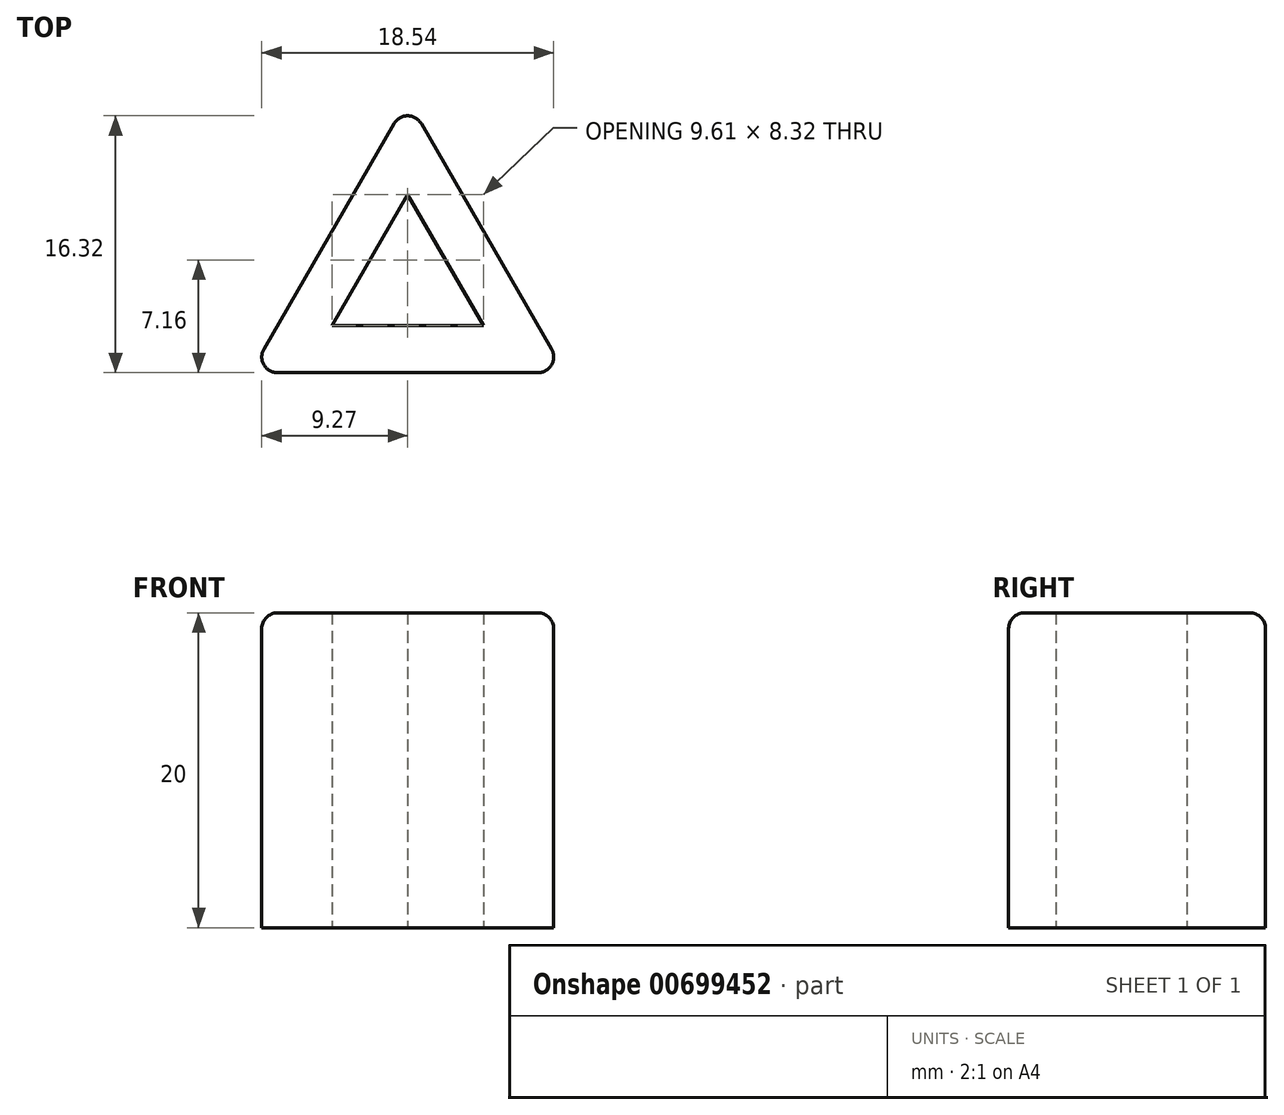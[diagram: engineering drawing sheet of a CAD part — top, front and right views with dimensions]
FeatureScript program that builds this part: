
annotation { "Feature Type Name" : "Feature", "Feature Type Description" : "" }
export const myFeature = defineFeature(function(context is Context, id is Id, definition is map)
    precondition{}
    {
        {
            var Q0;
            Q0=qCreatedBy(makeId("Top.planeOp"),FACE);
            var sketch = newSketch(context, id + "F0", { "sketchPlane" : qUnion([Q0])});
            skLineSegment(sketch, "E0.bottom", {"start": v(10, 10) * mm, "end": v(-10, 10) * mm, "construction": true});
            skLineSegment(sketch, "E0.top", {"start": v(10, -10) * mm, "end": v(-10, -10) * mm, "construction": true});
            skLineSegment(sketch, "E0.left", {"start": v(10, 10) * mm, "end": v(10, -10) * mm, "construction": true});
            skLineSegment(sketch, "E0.right", {"start": v(-10, 10) * mm, "end": v(-10, -10) * mm, "construction": true});
            skPoint(sketch, "E0.middle", {"position": v(0, 0) * mm});
            skLineSegment(sketch, "E1", {"start": v(0, 10) * mm, "end": v(-10, -7.32) * mm});
            skLineSegment(sketch, "E2", {"start": v(-10, -7.32) * mm, "end": v(10, -7.32) * mm});
            skLineSegment(sketch, "E3", {"start": v(10, -7.32) * mm, "end": v(0, 10) * mm});
            skLineSegment(sketch, "E4.0", {"start": v(0, 4) * mm, "end": v(-4.8, -4.32) * mm});
            skLineSegment(sketch, "E4.1", {"start": v(4.8, -4.32) * mm, "end": v(0, 4) * mm});
            skLineSegment(sketch, "E4.2", {"start": v(-4.8, -4.32) * mm, "end": v(4.8, -4.32) * mm});
            skSolve(sketch);
        }
        {
            var Q0;
            Q0 = qSketchRegion(id + "F0", true);
            extrude(context, id + "F1", {"entities" : qUnion([Q0]), "depth" : 20 * mm, "offsetDistance" : 25 * mm});
        }
        {
            var Q0;
            Q0=makeQuery(id+"F1.opExtrude","SWEPT_EDGE",EDGE,{"disambiguationData":[OSD([sQuery(id+"F0.wireOp",EDGE,"E1"),sQuery(id+"F0.wireOp",EDGE,"E2")])]});
            var Q1;
            Q1=makeQuery(id+"F1.opExtrude","CAP_EDGE",EDGE,{"disambiguationData":[OSD([sQuery(id+"F0.wireOp",EDGE,"E2")])],"isStart":false});
            var Q2;
            Q2=makeQuery(id+"F1.opExtrude","CAP_EDGE",EDGE,{"disambiguationData":[OSD([sQuery(id+"F0.wireOp",EDGE,"E1")])],"isStart":false});
            var Q3;
            Q3=makeQuery(id+"F1.opExtrude","CAP_EDGE",EDGE,{"disambiguationData":[OSD([sQuery(id+"F0.wireOp",EDGE,"E3")])],"isStart":false});
            var Q4;
            Q4=makeQuery(id+"F1.opExtrude","SWEPT_EDGE",EDGE,{"disambiguationData":[OSD([sQuery(id+"F0.wireOp",EDGE,"E2"),sQuery(id+"F0.wireOp",EDGE,"E3")])]});
            var Q5;
            Q5=makeQuery(id+"F1.opExtrude","SWEPT_EDGE",EDGE,{"disambiguationData":[OSD([sQuery(id+"F0.wireOp",EDGE,"E1"),sQuery(id+"F0.wireOp",EDGE,"E3")])]});
            fillet(context, id + "F2", {"entities" : qUnion([Q0, Q1, Q2, Q3, Q4, Q5]), "radius" : 1 * mm, "tangentPropagation" : true, "allowEdgeOverflow" : false});
        }
    });
